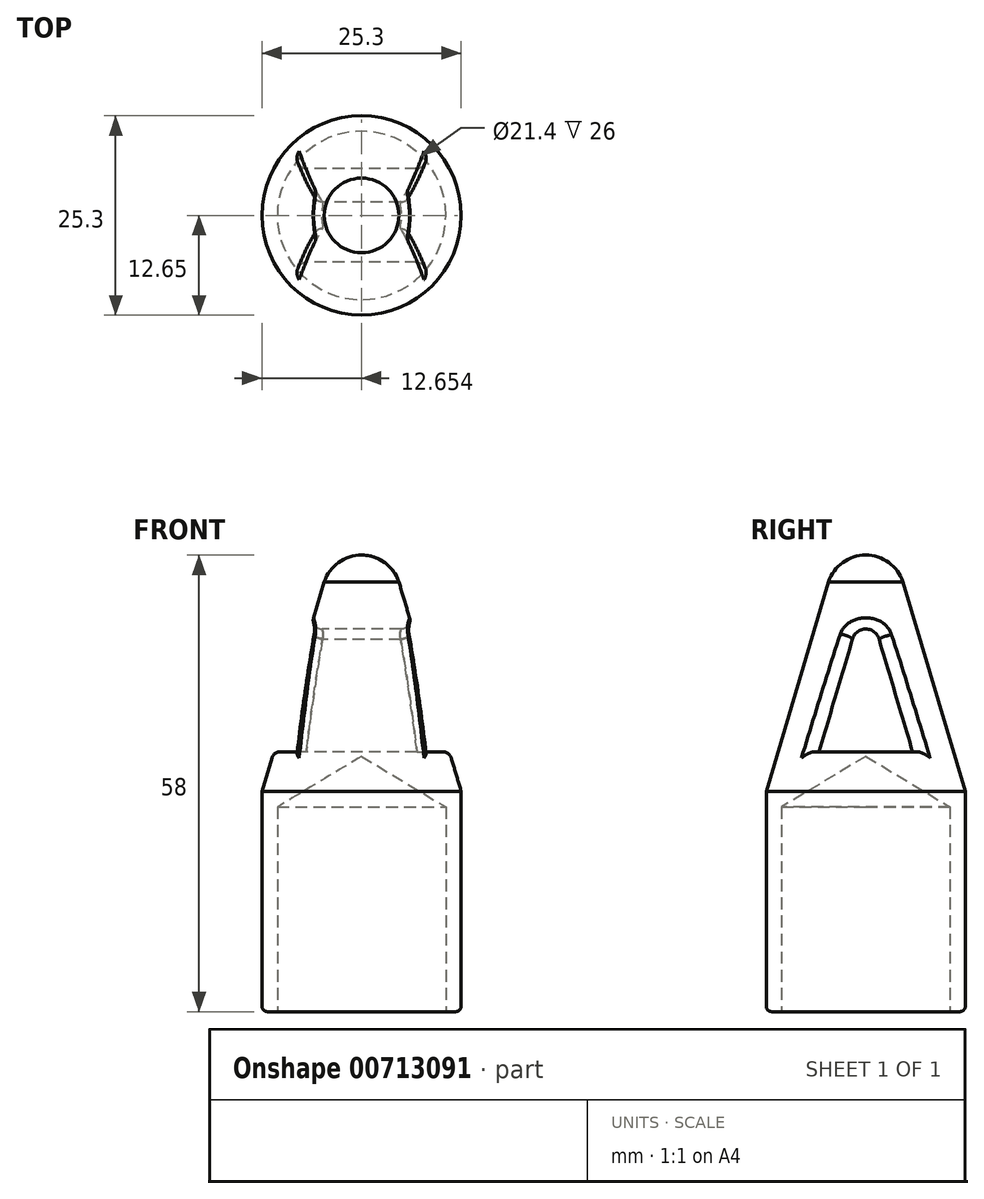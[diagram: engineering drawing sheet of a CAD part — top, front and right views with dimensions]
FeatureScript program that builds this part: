
annotation { "Feature Type Name" : "Feature", "Feature Type Description" : "" }
export const myFeature = defineFeature(function(context is Context, id is Id, definition is map)
    precondition{}
    {
        {
            var Q0;
            Q0=qCreatedBy(makeId("Front.planeOp"),FACE);
            var sketch = newSketch(context, id + "F0", { "sketchPlane" : qUnion([Q0])});
            skLineSegment(sketch, "E0.bottom", {"start": v(0.3, -10.32) * mm, "end": v(12.95, -10.32) * mm});
            skLineSegment(sketch, "E0.top", {"start": v(0.3, -38.32) * mm, "end": v(12.95, -38.32) * mm});
            skLineSegment(sketch, "E0.left", {"start": v(0.3, -10.32) * mm, "end": v(0.3, -38.32) * mm});
            skArc(sketch, "E1", {"start": v(12.95, 19.68) * mm, "mid": v(10.03, 18.74) * mm, "end": v(8.21, 16.27) * mm});
            skPoint(sketch, "E1.centerSnap0", {"position": v(12.95, -10.32) * mm});
            skLineSegment(sketch, "E2", {"start": v(0.3, -10.32) * mm, "end": v(8.21, 16.27) * mm});
            skPoint(sketch, "E0.right.start.orphan", {"position": v(25.6, -10.32) * mm});
            skLineSegment(sketch, "E3", {"start": v(12.95, 19.68) * mm, "end": v(12.95, -38.32) * mm});
            skPoint(sketch, "E4.start.orphan", {"position": v(12.95, 28.1) * mm});
            skSolve(sketch);
        }
        {
            var Q0;
            {var subQ0=sQuery(id+"F0.wireOp",EDGE,"E0.bottom");Q0=makeQuery(id+"F0.imprint","IMPRINT",FACE,{"disambiguationData":[TD([[makeQuery(id+"F0.imprint","IMPRINT",EDGE,{"derivedFrom":subQ0}),1.0]])]});}
            var Q1;
            {var subQ0=sQuery(id+"F0.wireOp",EDGE,"E0.bottom");Q1=makeQuery(id+"F0.imprint","IMPRINT",FACE,{"disambiguationData":[TD([[makeQuery(id+"F0.imprint","IMPRINT",EDGE,{"derivedFrom":subQ0}),-1.0]])]});}
            var Q2;
            Q2=sQuery(id+"F0.wireOp",EDGE,"E3");
            revolve(context, id + "F1", {"surfaceOperationType" : NewSurfaceOperationType.NEW, "entities" : qUnion([Q0, Q1]), "axis" : qUnion([Q2]), "revolveType" : RevolveType.FULL});
        }
        {
            var Q0;
            Q0=makeQuery(id+"F1.opRevolve","SWEPT_FACE",FACE,{"disambiguationData":[OSD([sQuery(id+"F0.wireOp",EDGE,"E0.top")])]});
            var sketch = newSketch(context, id + "F2", { "sketchPlane" : qUnion([Q0])});
            skPoint(sketch, "E5", {"position": v(12.95, 0) * mm});
            skSolve(sketch);
        }
        {
            var Q0;
            Q0=sQuery(id+"F2.wireOp",VERTEX,"E5");
            var Q1;
            Q1=makeQuery(id+"F1.opRevolve","SWEPT_BODY",BODY,{"disambiguationData":[OSD([sQuery(id+"F0.wireOp",EDGE,"E0.top"),sQuery(id+"F0.wireOp",EDGE,"E0.left"),sQuery(id+"F0.wireOp",EDGE,"E1"),sQuery(id+"F0.wireOp",EDGE,"E2"),sQuery(id+"F0.wireOp",EDGE,"E3")])]});
            hole(context, id + "F3", {"style" : HoleStyle.SIMPLE, "endStyle" : HoleEndStyle.BLIND, "holeDiameter" : 21.4 * mm, "majorDiameter" : 5 * mm, "holeDepth" : 26 * mm, "isTappedThrough" : true, "tappedDepth" : 12 * mm, "tapClearance" : 3, "startFromSketch" : true, "locations" : qUnion([Q0]), "scope" : qUnion([Q1])});
        }
        {
            var Q0;
            Q0=qCreatedBy(makeId("Right.planeOp"),FACE);
            var sketch = newSketch(context, id + "F4", { "sketchPlane" : qUnion([Q0])});
            skLineSegment(sketch, "E6.0", {"start": v(1.65, 9.14) * mm, "end": v(5.95, -5.32) * mm});
            skLineSegment(sketch, "E6.1", {"start": v(-5.95, -5.32) * mm, "end": v(-1.67, 9.06) * mm});
            skLineSegment(sketch, "E6.2", {"start": v(-5.95, -5.32) * mm, "end": v(5.95, -5.32) * mm});
            skPoint(sketch, "E7.first.point", {"position": v(-1.67, 9.06) * mm});
            skPoint(sketch, "E7.second.point", {"position": v(1.7, 8.96) * mm});
            skArc(sketch, "E8", {"start": v(1.7, 8.96) * mm, "mid": v(0.04, 10.3) * mm, "end": v(-1.68, 9.03) * mm});
            skPoint(sketch, "E8.third.point", {"position": v(0, 10.3) * mm});
            skSolve(sketch);
        }
        {
            var Q0;
            Q0 = qSketchRegion(id + "F4", true);
            extrude(context, id + "F5", {"entities" : qUnion([Q0]), "operationType" : NewBodyOperationType.REMOVE, "depth" : 25 * mm, "offsetDistance" : 25 * mm});
        }
        {
            var Q0;
            Q0=makeQuery(id+"F5.boolean.opBoolean","INTERSECT",EDGE,{"disambiguationData":[OD(0.0)],"derivedFrom":[makeQuery(id+"F1.opRevolve","SWEPT_FACE",FACE,{"disambiguationData":[OSD([sQuery(id+"F0.wireOp",EDGE,"E2")])]}),makeQuery(id+"F5.opExtrude","SWEPT_FACE",FACE,{"disambiguationData":[OSD([sQuery(id+"F4.wireOp",EDGE,"E6.0")])]})]});
            var Q1;
            Q1=makeQuery(id+"F5.boolean.opBoolean","INTERSECT",EDGE,{"disambiguationData":[OD(0.0)],"derivedFrom":[makeQuery(id+"F1.opRevolve","SWEPT_FACE",FACE,{"disambiguationData":[OSD([sQuery(id+"F0.wireOp",EDGE,"E2")])]}),makeQuery(id+"F5.opExtrude","SWEPT_FACE",FACE,{"disambiguationData":[OSD([sQuery(id+"F4.wireOp",EDGE,"E6.1")])]})]});
            var Q2;
            Q2=makeQuery(id+"F5.boolean.opBoolean","INTERSECT",EDGE,{"disambiguationData":[OD(0.0)],"derivedFrom":[makeQuery(id+"F1.opRevolve","SWEPT_FACE",FACE,{"disambiguationData":[OSD([sQuery(id+"F0.wireOp",EDGE,"E2")])]}),makeQuery(id+"F5.opExtrude","SWEPT_FACE",FACE,{"disambiguationData":[OSD([sQuery(id+"F4.wireOp",EDGE,"E6.2")])]})]});
            var Q3;
            Q3=makeQuery(id+"F5.boolean.opBoolean","INTERSECT",EDGE,{"disambiguationData":[OD(0.0)],"derivedFrom":[makeQuery(id+"F1.opRevolve","SWEPT_FACE",FACE,{"disambiguationData":[OSD([sQuery(id+"F0.wireOp",EDGE,"E2")])]}),makeQuery(id+"F5.opExtrude","SWEPT_FACE",FACE,{"disambiguationData":[OSD([sQuery(id+"F4.wireOp",EDGE,"E8")])]})]});
            var Q4;
            Q4=makeQuery(id+"F5.boolean.opBoolean","INTERSECT",EDGE,{"disambiguationData":[OD(1.0)],"derivedFrom":[makeQuery(id+"F1.opRevolve","SWEPT_FACE",FACE,{"disambiguationData":[OSD([sQuery(id+"F0.wireOp",EDGE,"E2")])]}),makeQuery(id+"F5.opExtrude","SWEPT_FACE",FACE,{"disambiguationData":[OSD([sQuery(id+"F4.wireOp",EDGE,"E6.1")])]})]});
            var Q5;
            Q5=makeQuery(id+"F5.boolean.opBoolean","INTERSECT",EDGE,{"disambiguationData":[OD(1.0)],"derivedFrom":[makeQuery(id+"F1.opRevolve","SWEPT_FACE",FACE,{"disambiguationData":[OSD([sQuery(id+"F0.wireOp",EDGE,"E2")])]}),makeQuery(id+"F5.opExtrude","SWEPT_FACE",FACE,{"disambiguationData":[OSD([sQuery(id+"F4.wireOp",EDGE,"E6.2")])]})]});
            var Q6;
            Q6=makeQuery(id+"F5.boolean.opBoolean","INTERSECT",EDGE,{"disambiguationData":[OD(1.0)],"derivedFrom":[makeQuery(id+"F1.opRevolve","SWEPT_FACE",FACE,{"disambiguationData":[OSD([sQuery(id+"F0.wireOp",EDGE,"E2")])]}),makeQuery(id+"F5.opExtrude","SWEPT_FACE",FACE,{"disambiguationData":[OSD([sQuery(id+"F4.wireOp",EDGE,"E6.0")])]})]});
            var Q7;
            Q7=makeQuery(id+"F5.boolean.opBoolean","INTERSECT",EDGE,{"disambiguationData":[OD(1.0)],"derivedFrom":[makeQuery(id+"F1.opRevolve","SWEPT_FACE",FACE,{"disambiguationData":[OSD([sQuery(id+"F0.wireOp",EDGE,"E2")])]}),makeQuery(id+"F5.opExtrude","SWEPT_FACE",FACE,{"disambiguationData":[OSD([sQuery(id+"F4.wireOp",EDGE,"E8")])]})]});
            fillet(context, id + "F6", {"entities" : qUnion([Q0, Q1, Q2, Q3, Q4, Q5, Q6, Q7]), "radius" : 1.1 * mm, "tangentPropagation" : true, "allowEdgeOverflow" : false});
        }
        {
            var Q0;
            Q0=makeQuery(id+"F1.opRevolve","SWEPT_EDGE",EDGE,{"disambiguationData":[OSD([sQuery(id+"F0.wireOp",EDGE,"E0.top"),sQuery(id+"F0.wireOp",EDGE,"E0.left")])]});
            fillet(context, id + "F7", {"entities" : qUnion([Q0]), "radius" : 0.7 * mm, "tangentPropagation" : true, "allowEdgeOverflow" : false});
        }
    });
